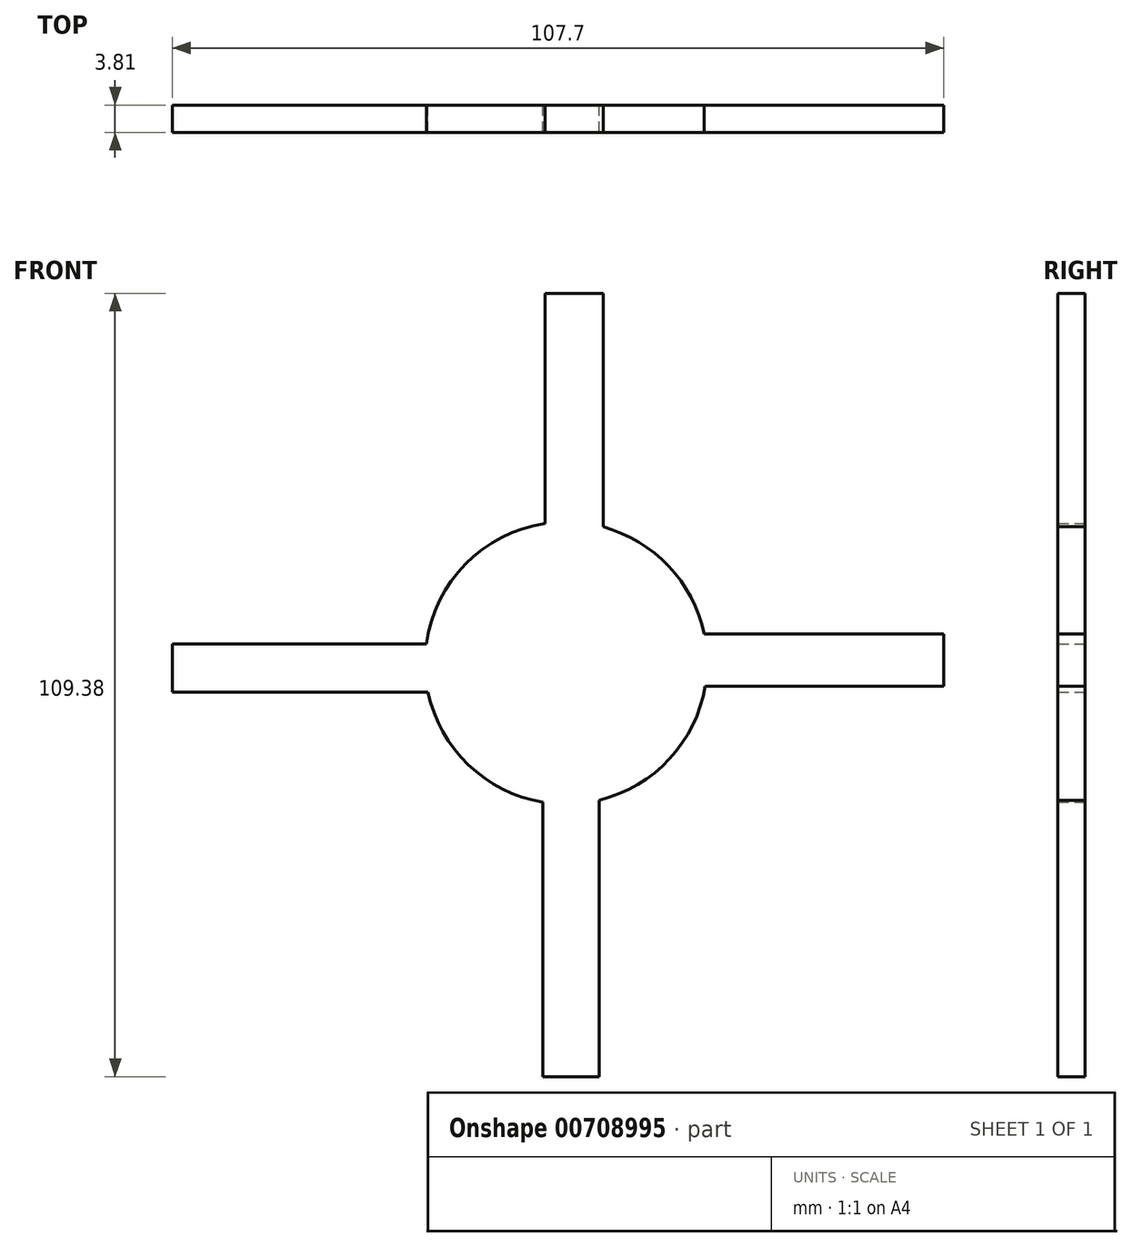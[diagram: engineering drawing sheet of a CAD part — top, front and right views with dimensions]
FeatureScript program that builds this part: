
annotation { "Feature Type Name" : "Feature", "Feature Type Description" : "" }
export const myFeature = defineFeature(function(context is Context, id is Id, definition is map)
    precondition{}
    {
        {
            var Q0;
            Q0=qCreatedBy(makeId("Front.planeOp"),FACE);
            var sketch = newSketch(context, id + "F0", { "sketchPlane" : qUnion([Q0])});
            skCircle(sketch, "E0", {"center": v(0, 0) * mm, "radius": 19.7 * mm});
            skLineSegment(sketch, "E1.bottom", {"start": v(-2.94, 11.89) * mm, "end": v(5.18, 11.89) * mm});
            skLineSegment(sketch, "E1.top", {"start": v(-2.94, 51.61) * mm, "end": v(5.18, 51.61) * mm});
            skLineSegment(sketch, "E1.left", {"start": v(-2.94, 11.89) * mm, "end": v(-2.94, 51.61) * mm});
            skLineSegment(sketch, "E1.right", {"start": v(5.18, 11.89) * mm, "end": v(5.18, 51.61) * mm});
            skLineSegment(sketch, "E2.bottom", {"start": v(11.05, 4.06) * mm, "end": v(52.73, 4.06) * mm});
            skLineSegment(sketch, "E2.top", {"start": v(11.05, -3.22) * mm, "end": v(52.73, -3.22) * mm});
            skLineSegment(sketch, "E2.left", {"start": v(11.05, 4.06) * mm, "end": v(11.05, -3.22) * mm});
            skLineSegment(sketch, "E2.right", {"start": v(52.73, 4.06) * mm, "end": v(52.73, -3.22) * mm});
            skLineSegment(sketch, "E3.bottom", {"start": v(-16.65, 2.66) * mm, "end": v(-54.97, 2.66) * mm});
            skLineSegment(sketch, "E3.top", {"start": v(-16.65, -4.06) * mm, "end": v(-54.97, -4.06) * mm});
            skLineSegment(sketch, "E3.left", {"start": v(-16.65, 2.66) * mm, "end": v(-16.65, -4.06) * mm});
            skLineSegment(sketch, "E3.right", {"start": v(-54.97, 2.66) * mm, "end": v(-54.97, -4.06) * mm});
            skLineSegment(sketch, "E4.bottom", {"start": v(-54.97, -4.06) * mm, "end": v(-35.39, -4.06) * mm});
            skLineSegment(sketch, "E5.bottom", {"start": v(-3.22, -13.57) * mm, "end": v(-4.34, -13.57) * mm});
            skLineSegment(sketch, "E5.top", {"start": v(-3.22, -48.82) * mm, "end": v(-4.34, -48.82) * mm});
            skLineSegment(sketch, "E6.left", {"start": v(-4.34, -48.82) * mm, "end": v(-4.34, -49.38) * mm});
            skLineSegment(sketch, "E6.right", {"start": v(4.34, -48.82) * mm, "end": v(4.34, -49.38) * mm});
            skLineSegment(sketch, "E7.bottom", {"start": v(-3.22, -13.57) * mm, "end": v(4.62, -13.57) * mm});
            skLineSegment(sketch, "E7.top", {"start": v(-3.22, -57.77) * mm, "end": v(4.62, -57.77) * mm});
            skLineSegment(sketch, "E7.left", {"start": v(-3.22, -13.57) * mm, "end": v(-3.22, -57.77) * mm});
            skLineSegment(sketch, "E7.right", {"start": v(4.62, -13.57) * mm, "end": v(4.62, -57.77) * mm});
            skSolve(sketch);
        }
        {
            var Q0;
            {var subQ5=sQuery(id+"F0.wireOp",EDGE,"E1.top");Q0=makeQuery(id+"F0.imprint","IMPRINT",FACE,{"disambiguationData":[TD([[makeQuery(id+"F0.imprint","IMPRINT",EDGE,{"derivedFrom":subQ5}),-1.0]])]});}
            var Q1;
            {var subQ5=sQuery(id+"F0.wireOp",EDGE,"E1.bottom");Q1=makeQuery(id+"F0.imprint","IMPRINT",FACE,{"disambiguationData":[TD([[makeQuery(id+"F0.imprint","IMPRINT",EDGE,{"derivedFrom":subQ5}),1.0]])]});}
            var Q2;
            {var subQ7=sQuery(id+"F0.wireOp",EDGE,"E1.bottom");Q2=makeQuery(id+"F0.imprint","IMPRINT",FACE,{"disambiguationData":[TD([[makeQuery(id+"F0.imprint","IMPRINT",EDGE,{"derivedFrom":subQ7}),-1.0]])]});}
            var Q3;
            {var subQ0=sQuery(id+"F0.wireOp",EDGE,"E3.right");Q3=makeQuery(id+"F0.imprint","IMPRINT",FACE,{"disambiguationData":[TD([[makeQuery(id+"F0.imprint","IMPRINT",EDGE,{"derivedFrom":subQ0}),1.0]])]});}
            var Q4;
            {var subQ5=sQuery(id+"F0.wireOp",EDGE,"E3.left");Q4=makeQuery(id+"F0.imprint","IMPRINT",FACE,{"disambiguationData":[TD([[makeQuery(id+"F0.imprint","IMPRINT",EDGE,{"derivedFrom":subQ5}),-1.0]])]});}
            var Q5;
            {var subQ5=sQuery(id+"F0.wireOp",EDGE,"E2.left");Q5=makeQuery(id+"F0.imprint","IMPRINT",FACE,{"disambiguationData":[TD([[makeQuery(id+"F0.imprint","IMPRINT",EDGE,{"derivedFrom":subQ5}),1.0]])]});}
            var Q6;
            {var subQ5=sQuery(id+"F0.wireOp",EDGE,"E2.right");Q6=makeQuery(id+"F0.imprint","IMPRINT",FACE,{"disambiguationData":[TD([[makeQuery(id+"F0.imprint","IMPRINT",EDGE,{"derivedFrom":subQ5}),-1.0]])]});}
            var Q7;
            {var subQ5=sQuery(id+"F0.wireOp",EDGE,"E7.bottom");Q7=makeQuery(id+"F0.imprint","IMPRINT",FACE,{"disambiguationData":[TD([[makeQuery(id+"F0.imprint","IMPRINT",EDGE,{"derivedFrom":subQ5}),-1.0]])]});}
            var Q8;
            {var subQ2=sQuery(id+"F0.wireOp",EDGE,"E7.top");Q8=makeQuery(id+"F0.imprint","IMPRINT",FACE,{"disambiguationData":[TD([[makeQuery(id+"F0.imprint","IMPRINT",EDGE,{"derivedFrom":subQ2}),1.0]])]});}
            extrude(context, id + "F1", {"entities" : qUnion([Q0, Q1, Q2, Q3, Q4, Q5, Q6, Q7, Q8]), "depth" : 3.8 * mm, "offsetDistance" : 25.4 * mm});
        }
    });
